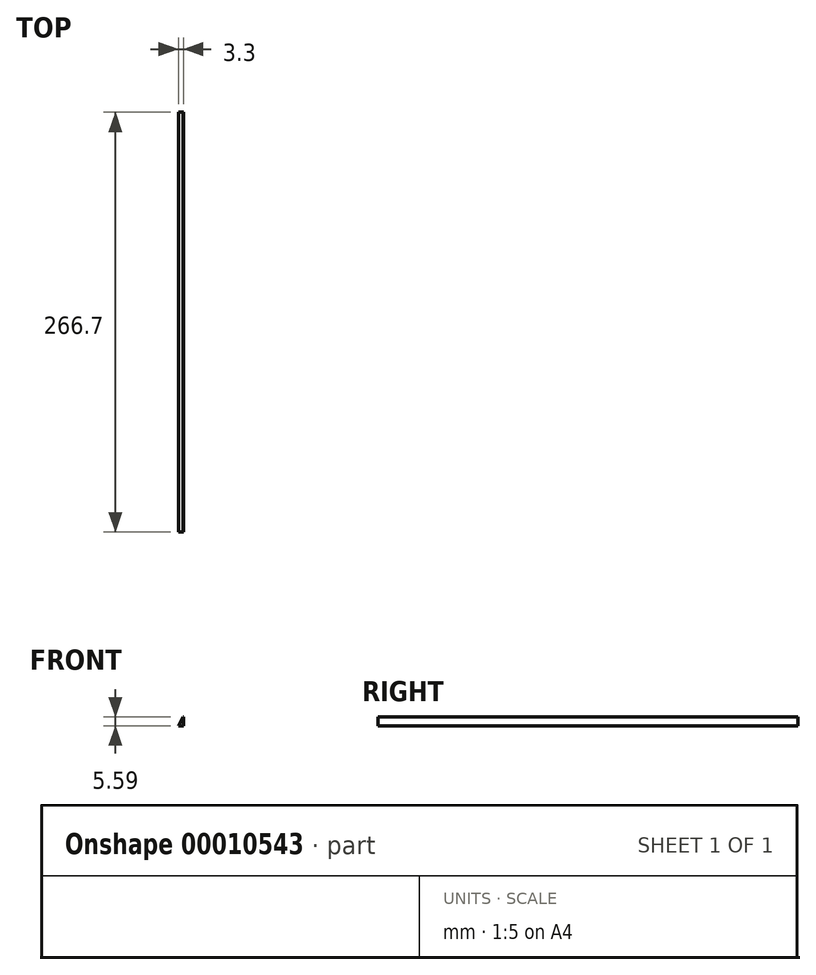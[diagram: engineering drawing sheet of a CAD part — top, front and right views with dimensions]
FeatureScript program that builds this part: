
annotation { "Feature Type Name" : "Feature", "Feature Type Description" : "" }
export const myFeature = defineFeature(function(context is Context, id is Id, definition is map)
    precondition{}
    {
        {
            var Q0;
            Q0=qCreatedBy(makeId("Front.planeOp"),FACE);
            var sketch = newSketch(context, id + "F0", { "sketchPlane" : qUnion([Q0])});
            skLineSegment(sketch, "E0", {"start": v(0, 0) * mm, "end": v(3.3, 0) * mm});
            skLineSegment(sketch, "E1", {"start": v(3.3, 0) * mm, "end": v(3.3, 5.59) * mm});
            skLineSegment(sketch, "E2", {"start": v(2.9, 5.59) * mm, "end": v(0, 0) * mm});
            skLineSegment(sketch, "E3", {"start": v(3.3, 5.59) * mm, "end": v(2.9, 5.59) * mm});
            skPoint(sketch, "E4.orphan", {"position": v(3.3, 6.35) * mm});
            skSolve(sketch);
        }
        {
            var Q0;
            Q0 = qSketchRegion(id + "F0", true);
            extrude(context, id + "F1", {"entities" : qUnion([Q0]), "depth" : 266.7 * mm, "symmetric" : true});
        }
    });
